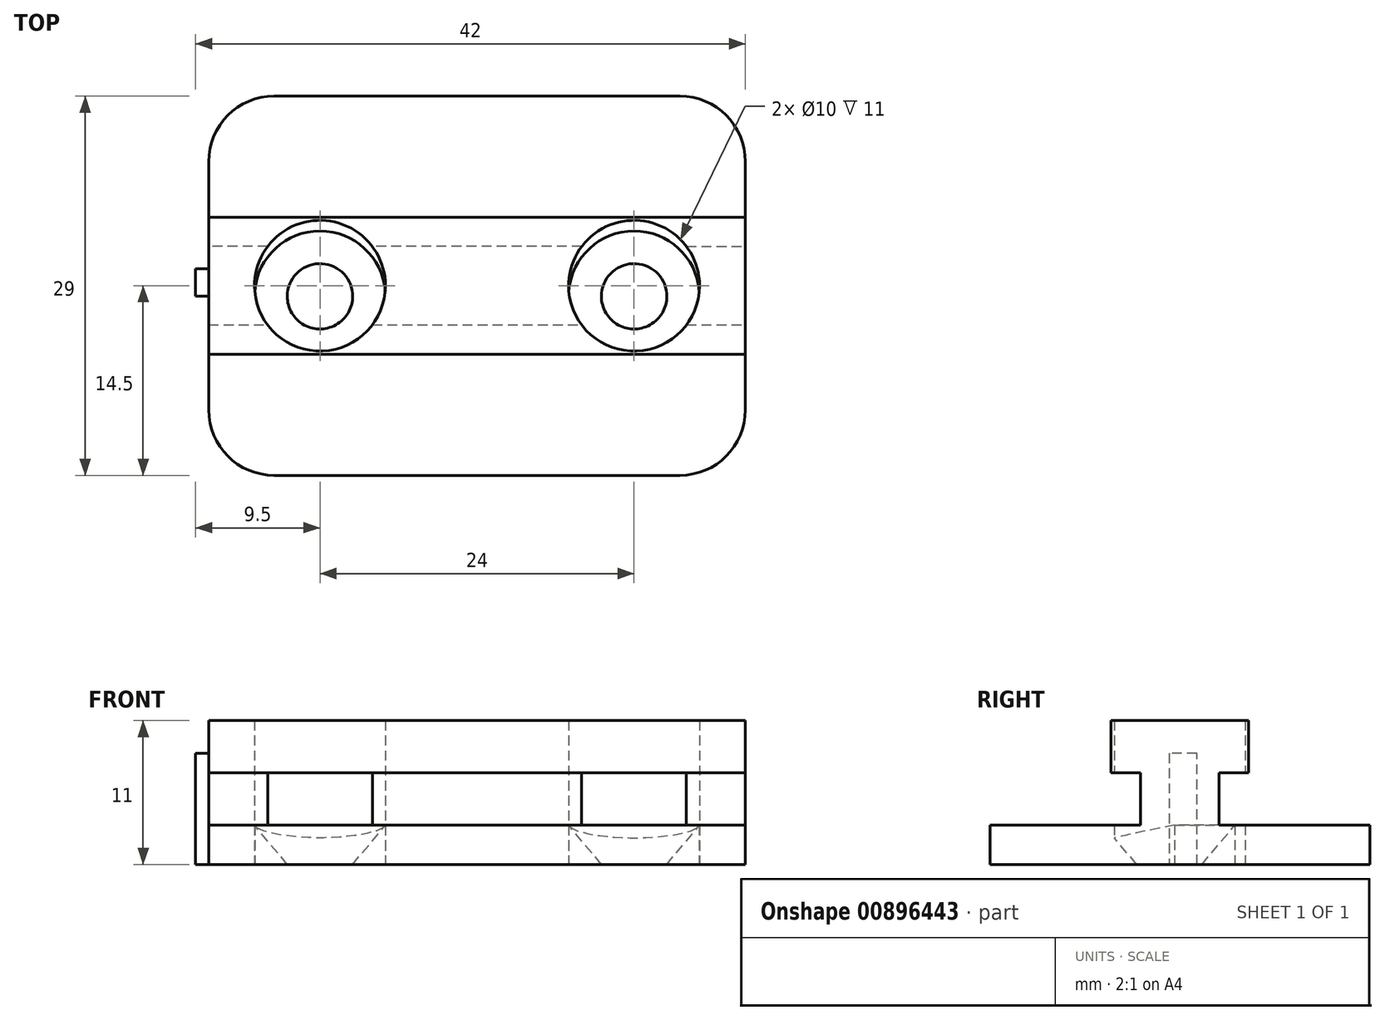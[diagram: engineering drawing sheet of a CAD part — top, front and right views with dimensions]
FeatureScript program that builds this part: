
annotation { "Feature Type Name" : "Feature", "Feature Type Description" : "" }
export const myFeature = defineFeature(function(context is Context, id is Id, definition is map)
    precondition{}
    {
        {
            var Q0;
            Q0=qCreatedBy(makeId("Top.planeOp"),FACE);
            var sketch = newSketch(context, id + "F0", { "sketchPlane" : qUnion([Q0])});
            skPoint(sketch, "E0.endSnap0", {"position": v(41, -14.5) * mm});
            skCircle(sketch, "E1", {"center": v(32.5, -14.5) * mm, "radius": 5 * mm});
            skCircle(sketch, "E2", {"center": v(36, -24) * mm, "radius": 5 * mm});
            skLineSegment(sketch, "E3", {"start": v(5, -29) * mm, "end": v(5, -24) * mm});
            skCircle(sketch, "E4", {"center": v(5, -24) * mm, "radius": 5 * mm});
            skLineSegment(sketch, "E5", {"start": v(0, -5) * mm, "end": v(5, -5) * mm});
            skCircle(sketch, "E6", {"center": v(5, -5) * mm, "radius": 5 * mm});
            skLineSegment(sketch, "E7", {"start": v(41, -5) * mm, "end": v(36, -5) * mm});
            skCircle(sketch, "E8", {"center": v(36, -5) * mm, "radius": 5 * mm});
            skLineSegment(sketch, "E9", {"start": v(5, -29) * mm, "end": v(36, -29) * mm});
            skLineSegment(sketch, "E10", {"start": v(41, -5) * mm, "end": v(41, -24) * mm});
            skLineSegment(sketch, "E11", {"start": v(0, -5) * mm, "end": v(0, -24) * mm});
            skLineSegment(sketch, "E12", {"start": v(36, -5) * mm, "end": v(36, 0) * mm});
            skLineSegment(sketch, "E13", {"start": v(36, 0) * mm, "end": v(5, 0) * mm});
            skLineSegment(sketch, "E14", {"start": v(0, -24) * mm, "end": v(0, -14.5) * mm});
            skCircle(sketch, "E15", {"center": v(8.5, -14.5) * mm, "radius": 5 * mm});
            skSolve(sketch);
        }
        {
            var Q0;
            Q0 = qSketchRegion(id + "F0", true);
            extrude(context, id + "F1", {"entities" : qUnion([Q0]), "depth" : 3 * mm, "offsetDistance" : 25 * mm});
        }
        {
            var Q0;
            Q0=makeQuery(id+"F1.opExtrude","CAP_FACE",FACE,{"disambiguationData":[OSD([sQuery(id+"F0.wireOp",EDGE,"E1"),sQuery(id+"F0.wireOp",EDGE,"E2"),sQuery(id+"F0.wireOp",EDGE,"E4"),sQuery(id+"F0.wireOp",EDGE,"E6"),sQuery(id+"F0.wireOp",EDGE,"E8"),sQuery(id+"F0.wireOp",EDGE,"E9"),sQuery(id+"F0.wireOp",EDGE,"E10"),sQuery(id+"F0.wireOp",EDGE,"E11"),sQuery(id+"F0.wireOp",EDGE,"E13"),sQuery(id+"F0.wireOp",EDGE,"E14"),sQuery(id+"F0.wireOp",EDGE,"E15")])],"isStart":false});
            var sketch = newSketch(context, id + "F2", { "sketchPlane" : qUnion([Q0])});
            skLineSegment(sketch, "E16", {"start": v(0, -14.5) * mm, "end": v(0, -11.5) * mm});
            skLineSegment(sketch, "E17", {"start": v(0, -14.5) * mm, "end": v(0, -17.5) * mm});
            skLineSegment(sketch, "E18", {"start": v(41, -11.5) * mm, "end": v(41, -17.5) * mm});
            skLineSegment(sketch, "E19", {"start": v(36.5, -11.5) * mm, "end": v(41, -11.5) * mm});
            skLineSegment(sketch, "E20", {"start": v(28.5, -11.5) * mm, "end": v(12.5, -11.5) * mm});
            skLineSegment(sketch, "E21", {"start": v(4.5, -11.5) * mm, "end": v(0, -11.5) * mm});
            skLineSegment(sketch, "E22", {"start": v(0, -17.5) * mm, "end": v(4.5, -17.5) * mm});
            skLineSegment(sketch, "E23", {"start": v(12.5, -17.5) * mm, "end": v(28.5, -17.5) * mm});
            skLineSegment(sketch, "E24", {"start": v(36.5, -17.5) * mm, "end": v(41, -17.5) * mm});
            skLineSegment(sketch, "E25", {"start": v(0, -14.5) * mm, "end": v(3.5, -14.5) * mm});
            skLineSegment(sketch, "E26", {"start": v(3.5, -14.5) * mm, "end": v(3.5, -11.5) * mm});
            skLineSegment(sketch, "E27", {"start": v(3.5, -11.5) * mm, "end": v(3.5, -17.5) * mm});
            skLineSegment(sketch, "E28", {"start": v(41, -14.5) * mm, "end": v(37.5, -14.5) * mm});
            skLineSegment(sketch, "E29", {"start": v(37.5, -14.5) * mm, "end": v(37.5, -11.5) * mm});
            skLineSegment(sketch, "E30", {"start": v(37.5, -11.5) * mm, "end": v(37.5, -17.5) * mm});
            skArc(sketch, "E31", {"start": v(3.5, -14.5) * mm, "mid": v(3.76, -12.92) * mm, "end": v(4.5, -11.5) * mm});
            skArc(sketch, "E32", {"start": v(4.5, -17.5) * mm, "mid": v(3.76, -16.08) * mm, "end": v(3.5, -14.5) * mm});
            skArc(sketch, "E33", {"start": v(12.5, -11.5) * mm, "mid": v(13.5, -14.5) * mm, "end": v(12.5, -17.5) * mm});
            skArc(sketch, "E34", {"start": v(28.5, -11.5) * mm, "mid": v(27.5, -14.5) * mm, "end": v(28.5, -17.5) * mm});
            skArc(sketch, "E35", {"start": v(36.5, -11.5) * mm, "mid": v(37.5, -14.5) * mm, "end": v(36.5, -17.5) * mm});
            skSolve(sketch);
        }
        {
            var Q0;
            Q0 = qSketchRegion(id + "F2", true);
            extrude(context, id + "F3", {"entities" : qUnion([Q0]), "operationType" : NewBodyOperationType.ADD, "depth" : 4 * mm, "offsetDistance" : 25 * mm});
        }
        {
            var Q0;
            Q0=makeQuery(id+"F3.opExtrude","CAP_FACE",FACE,{"disambiguationData":[OSD([sQuery(id+"F2.wireOp",EDGE,"E20"),sQuery(id+"F2.wireOp",EDGE,"E23"),sQuery(id+"F2.wireOp",EDGE,"E33"),sQuery(id+"F2.wireOp",EDGE,"E34")])],"isStart":false});
            var sketch = newSketch(context, id + "F4", { "sketchPlane" : qUnion([Q0])});
            skLineSegment(sketch, "E36", {"start": v(8.5, -14.5) * mm, "end": v(0, -14.5) * mm});
            skLineSegment(sketch, "E37", {"start": v(0, -14.5) * mm, "end": v(0, -9.25) * mm});
            skLineSegment(sketch, "E38", {"start": v(0, -14.5) * mm, "end": v(0, -19.75) * mm});
            skLineSegment(sketch, "E39", {"start": v(0, -9.25) * mm, "end": v(0, -19.75) * mm});
            skLineSegment(sketch, "E40", {"start": v(41, -19.75) * mm, "end": v(0, -19.75) * mm});
            skLineSegment(sketch, "E41", {"start": v(0, -9.25) * mm, "end": v(41, -9.25) * mm});
            skLineSegment(sketch, "E42", {"start": v(41, -9.25) * mm, "end": v(41, -19.75) * mm});
            skCircle(sketch, "E43", {"center": v(8.5, -14.5) * mm, "radius": 5 * mm});
            skCircle(sketch, "E44", {"center": v(32.5, -14.5) * mm, "radius": 5 * mm});
            skSolve(sketch);
        }
        {
            var Q0;
            Q0 = qSketchRegion(id + "F4", true);
            extrude(context, id + "F5", {"entities" : qUnion([Q0]), "operationType" : NewBodyOperationType.ADD, "depth" : 4 * mm, "offsetDistance" : 25 * mm});
        }
        {
            var Q0;
            Q0=makeQuery(id+"F5.boolean.opBoolean","MERGE",FACE,{"derivedFrom":[makeQuery(id+"F3.boolean.opBoolean","MERGE",FACE,{"derivedFrom":[makeQuery(id+"F1.opExtrude","SWEPT_FACE",FACE,{"disambiguationData":[OSD([sQuery(id+"F0.wireOp",EDGE,"E11"),sQuery(id+"F0.wireOp",EDGE,"E14")])]}),makeQuery(id+"F3.opExtrude","SWEPT_FACE",FACE,{"disambiguationData":[OSD([sQuery(id+"F2.wireOp",EDGE,"E16"),sQuery(id+"F2.wireOp",EDGE,"E17")])]})]}),makeQuery(id+"F5.opExtrude","SWEPT_FACE",FACE,{"disambiguationData":[OSD([sQuery(id+"F4.wireOp",EDGE,"E39")])]})]});
            var sketch = newSketch(context, id + "F6", { "sketchPlane" : qUnion([Q0])});
            skLineSegment(sketch, "E45", {"start": v(14.5, 0) * mm, "end": v(13.2, 0) * mm});
            skLineSegment(sketch, "E46", {"start": v(13.2, 0) * mm, "end": v(13.2, 8.5) * mm});
            skLineSegment(sketch, "E47", {"start": v(13.2, 8.5) * mm, "end": v(15.3, 8.5) * mm});
            skLineSegment(sketch, "E48", {"start": v(15.3, 8.5) * mm, "end": v(15.3, 0) * mm});
            skLineSegment(sketch, "E49", {"start": v(13.2, 0) * mm, "end": v(15.3, 0) * mm});
            skSolve(sketch);
        }
        {
            var Q0;
            Q0 = qSketchRegion(id + "F6", true);
            extrude(context, id + "F7", {"entities" : qUnion([Q0]), "operationType" : NewBodyOperationType.ADD, "depth" : 1 * mm, "offsetDistance" : 25 * mm});
        }
        {
            var Q0;
            Q0=makeQuery(id+"F7.opExtrude","SWEPT_FACE",FACE,{"disambiguationData":[OSD([sQuery(id+"F6.wireOp",EDGE,"E48")])]});
            var sketch = newSketch(context, id + "F8", { "sketchPlane" : qUnion([Q0])});
            skLineSegment(sketch, "E50", {"start": v(3.5, 0) * mm, "end": v(6, 0) * mm});
            skLineSegment(sketch, "E51", {"start": v(8.5, 0) * mm, "end": v(8.5, 5.32) * mm});
            skLineSegment(sketch, "E52", {"start": v(6, 0) * mm, "end": v(3.5, 3) * mm});
            skLineSegment(sketch, "E53", {"start": v(3.5, 0) * mm, "end": v(3.5, 3) * mm});
            skLineSegment(sketch, "E54", {"start": v(37.5, 0) * mm, "end": v(35, 0) * mm});
            skLineSegment(sketch, "E55", {"start": v(32.5, 0) * mm, "end": v(32.5, 5.87) * mm});
            skLineSegment(sketch, "E56", {"start": v(37.5, 0) * mm, "end": v(37.5, 3) * mm});
            skLineSegment(sketch, "E57", {"start": v(37.5, 3) * mm, "end": v(35, 0) * mm});
            skSolve(sketch);
        }
        {
            var Q0;
            Q0 = qSketchRegion(id + "F6", true);
            extrude(context, id + "F9", {"entities" : qUnion([Q0]), "operationType" : NewBodyOperationType.ADD, "depth" : 0.8 * mm, "offsetDistance" : 25 * mm});
        }
        {
            var Q0;
            Q0=makeQuery(id+"F8.imprint","IMPRINT",FACE,{"disambiguationData":[TD([[makeQuery(id+"F8.imprint","IMPRINT",EDGE,{"derivedFrom":sQuery(id+"F8.wireOp",EDGE,"E50")}),1.0]])]});
            var Q1;
            Q1=sQuery(id+"F8.wireOp",EDGE,"E51");
            revolve(context, id + "F10", {"operationType" : NewBodyOperationType.ADD, "surfaceOperationType" : NewSurfaceOperationType.NEW, "entities" : qUnion([Q0]), "axis" : qUnion([Q1]), "revolveType" : RevolveType.FULL});
        }
        {
            var Q0;
            Q0=makeQuery(id+"F8.imprint","IMPRINT",FACE,{"disambiguationData":[TD([[makeQuery(id+"F8.imprint","IMPRINT",EDGE,{"derivedFrom":sQuery(id+"F8.wireOp",EDGE,"E54")}),-1.0]])]});
            var Q1;
            Q1=sQuery(id+"F8.wireOp",EDGE,"E55");
            revolve(context, id + "F11", {"operationType" : NewBodyOperationType.ADD, "surfaceOperationType" : NewSurfaceOperationType.NEW, "entities" : qUnion([Q0]), "axis" : qUnion([Q1]), "revolveType" : RevolveType.FULL});
        }
    });
